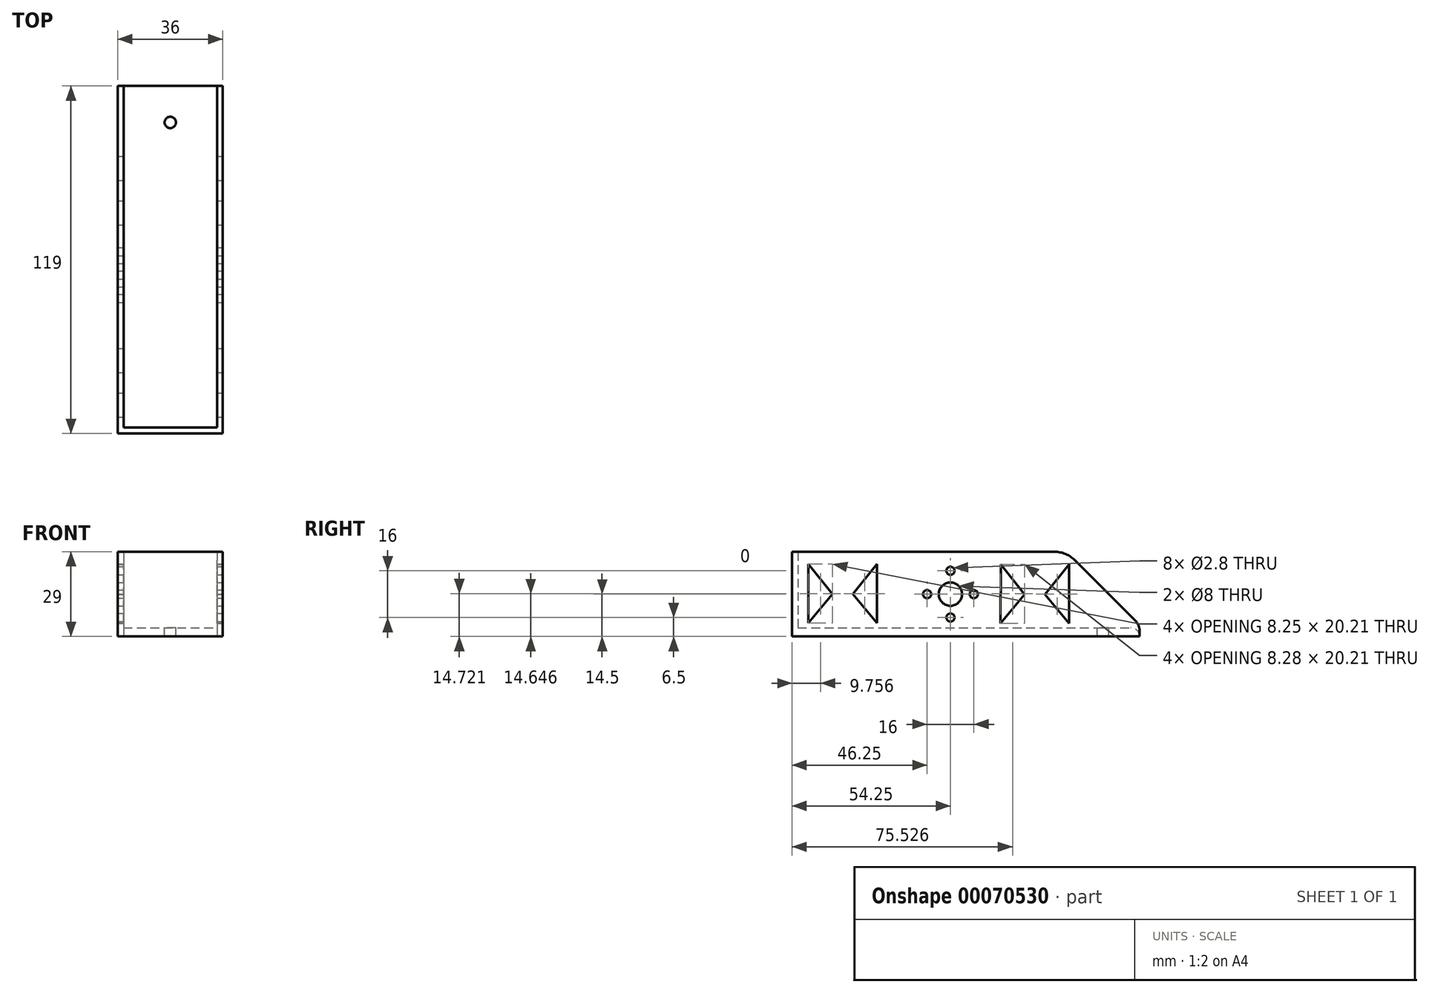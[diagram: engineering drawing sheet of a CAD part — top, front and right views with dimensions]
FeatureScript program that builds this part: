
annotation { "Feature Type Name" : "Feature", "Feature Type Description" : "" }
export const myFeature = defineFeature(function(context is Context, id is Id, definition is map)
    precondition{}
    {
        {
            var Q0;
            Q0=qCreatedBy(makeId("Top.planeOp"),FACE);
            var sketch = newSketch(context, id + "F0", { "sketchPlane" : qUnion([Q0])});
            skLineSegment(sketch, "E0.rect.bottom", {"start": v(-18, -59.5) * mm, "end": v(18, -59.5) * mm});
            skLineSegment(sketch, "E0.rect.top", {"start": v(-18, 59.5) * mm, "end": v(18, 59.5) * mm});
            skLineSegment(sketch, "E0.rect.left", {"start": v(-18, -59.5) * mm, "end": v(-18, 59.5) * mm});
            skLineSegment(sketch, "E0.rect.right", {"start": v(18, -59.5) * mm, "end": v(18, 59.5) * mm});
            skPoint(sketch, "E0.rect.middle", {"position": v(0, 0) * mm});
            skSolve(sketch);
        }
        {
            var Q0;
            Q0=makeQuery(id+"F0.imprint","IMPRINT",FACE,{"disambiguationData":[TD([[makeQuery(id+"F0.imprint","IMPRINT",EDGE,{"derivedFrom":sQuery(id+"F0.wireOp",EDGE,"E0.rect.bottom")}),1.0]])]});
            extrude(context, id + "F1", {"entities" : qUnion([Q0]), "depth" : 3 * mm});
        }
        {
            var Q0;
            Q0=makeQuery(id+"F1.opExtrude","CAP_FACE",FACE,{"disambiguationData":[OSD([sQuery(id+"F0.wireOp",EDGE,"E0.rect.bottom"),sQuery(id+"F0.wireOp",EDGE,"E0.rect.top"),sQuery(id+"F0.wireOp",EDGE,"E0.rect.left"),sQuery(id+"F0.wireOp",EDGE,"E0.rect.right")])],"isStart":false});
            var sketch = newSketch(context, id + "F2", { "sketchPlane" : qUnion([Q0])});
            skLineSegment(sketch, "E1.rect.bottom", {"start": v(-16, -57.5) * mm, "end": v(16, -57.5) * mm});
            skLineSegment(sketch, "E1.rect.left", {"start": v(-16, -57.5) * mm, "end": v(-16, 57.5) * mm});
            skLineSegment(sketch, "E1.rect.right", {"start": v(16, -57.5) * mm, "end": v(16, 57.5) * mm});
            skPoint(sketch, "E1.rect.middle", {"position": v(0, 0) * mm});
            skPoint(sketch, "E2.endSnap0", {"position": v(0, -57.5) * mm});
            skLineSegment(sketch, "E3", {"start": v(16, 57.5) * mm, "end": v(16, 59.5) * mm});
            skLineSegment(sketch, "E4", {"start": v(-16, 57.5) * mm, "end": v(-16, 59.5) * mm});
            skSolve(sketch);
        }
        {
            var Q0;
            Q0=makeQuery(id+"F2.imprint","IMPRINT",FACE,{"disambiguationData":[TD([[makeQuery(id+"F2.imprint","IMPRINT",EDGE,{"derivedFrom":sQuery(id+"F2.wireOp",EDGE,"E1.rect.bottom")}),-1.0]])]});
            extrude(context, id + "F3", {"entities" : qUnion([Q0]), "operationType" : NewBodyOperationType.ADD, "depth" : 26 * mm});
        }
        {
            var Q0;
            Q0=makeQuery(id+"F1.opExtrude","CAP_FACE",FACE,{"disambiguationData":[OSD([sQuery(id+"F0.wireOp",EDGE,"E0.rect.bottom"),sQuery(id+"F0.wireOp",EDGE,"E0.rect.top"),sQuery(id+"F0.wireOp",EDGE,"E0.rect.left"),sQuery(id+"F0.wireOp",EDGE,"E0.rect.right")])],"isStart":false});
            var sketch = newSketch(context, id + "F4", { "sketchPlane" : qUnion([Q0])});
            skLineSegment(sketch, "E5", {"start": v(0, -57.5) * mm, "end": v(0, 47) * mm, "construction": true});
            skPoint(sketch, "E5.endSnap0", {"position": v(0, -57.5) * mm});
            skArc(sketch, "E6", {"start": v(-3.7, 45.5) * mm, "mid": v(0, 43) * mm, "end": v(3.7, 45.5) * mm});
            skCircle(sketch, "E7", {"center": v(0, 47) * mm, "radius": 1.95 * mm});
            skLineSegment(sketch, "E8.rect.bottom", {"start": v(-4, 45.5) * mm, "end": v(-1.25, 45.5) * mm});
            skLineSegment(sketch, "E8.rect.top", {"start": v(-4, 48.5) * mm, "end": v(-1.25, 48.5) * mm});
            skLineSegment(sketch, "E8.rect.left", {"start": v(-4, 45.5) * mm, "end": v(-4, 48.5) * mm});
            skLineSegment(sketch, "E8.rect.right", {"start": v(4, 45.5) * mm, "end": v(4, 48.5) * mm});
            skArc(sketch, "E9.trimOffspring", {"start": v(3.7, 48.5) * mm, "mid": v(0, 51) * mm, "end": v(-3.7, 48.5) * mm});
            skLineSegment(sketch, "E10.trimOffspring", {"start": v(1.25, 45.5) * mm, "end": v(4, 45.5) * mm});
            skLineSegment(sketch, "E11.trimOffspring", {"start": v(1.25, 48.5) * mm, "end": v(4, 48.5) * mm});
            skSolve(sketch);
        }
        {
            var Q0;
            {var subQ0=sQuery(id+"F0.wireOp",EDGE,"E0.rect.top");var subQ1=makeQuery(id+"F1.opExtrude","CAP_EDGE",EDGE,{"disambiguationData":[OSD([subQ0])],"isStart":false});Q0=makeQuery(id+"F3.opExtrude","CAP_EDGE",EDGE,{"disambiguationData":[OSD([subQ0]),TDD([makeQuery(id+"F2.imprint","IMPRINT",EDGE,{"disambiguationData":[TD([[makeQuery(id+"F2.imprint","INTERSECT",VERTEX,{"derivedFrom":[subQ1,makeQuery(id+"F1.opExtrude","CAP_EDGE",EDGE,{"disambiguationData":[OSD([sQuery(id+"F0.wireOp",EDGE,"E0.rect.left")])],"isStart":false})]}),-1.0]])],"derivedFrom":subQ1})])],"isStart":false});}
            var Q1;
            {var subQ0=sQuery(id+"F0.wireOp",EDGE,"E0.rect.top");var subQ1=makeQuery(id+"F1.opExtrude","CAP_EDGE",EDGE,{"disambiguationData":[OSD([subQ0])],"isStart":false});Q1=makeQuery(id+"F3.opExtrude","CAP_EDGE",EDGE,{"disambiguationData":[OSD([subQ0]),TDD([makeQuery(id+"F2.imprint","IMPRINT",EDGE,{"disambiguationData":[TD([[makeQuery(id+"F2.imprint","INTERSECT",VERTEX,{"derivedFrom":[subQ1,makeQuery(id+"F1.opExtrude","CAP_EDGE",EDGE,{"disambiguationData":[OSD([sQuery(id+"F0.wireOp",EDGE,"E0.rect.right")])],"isStart":false})]}),1.0]])],"derivedFrom":subQ1})])],"isStart":false});}
            chamfer(context, id + "F5", {"entities" : qUnion([Q0, Q1]), "width" : 25 * mm, "tangentPropagation" : true});
        }
        {
            var Q0;
            {var subQ0=sQuery(id+"F2.wireOp",EDGE,"E3");var subQ1=sQuery(id+"F0.wireOp",EDGE,"E0.rect.right");var subQ2=sQuery(id+"F0.wireOp",EDGE,"E0.rect.top");var subQ3=makeQuery(id+"F1.opExtrude","CAP_EDGE",EDGE,{"disambiguationData":[OSD([subQ2])],"isStart":false});Q0=makeQuery(id+"F5.opChamfer","BLEND_EDGE",EDGE,{"blendedFrom":[makeQuery(id+"F3.opExtrude","CAP_EDGE",EDGE,{"disambiguationData":[OSD([subQ2]),TDD([makeQuery(id+"F2.imprint","IMPRINT",EDGE,{"disambiguationData":[TD([[makeQuery(id+"F2.imprint","INTERSECT",VERTEX,{"derivedFrom":[subQ3,makeQuery(id+"F1.opExtrude","CAP_EDGE",EDGE,{"disambiguationData":[OSD([subQ1])],"isStart":false})]}),1.0]])],"derivedFrom":subQ3})])],"isStart":false}),makeQuery(id+"F3.opExtrude","CAP_FACE",FACE,{"disambiguationData":[OSD([sQuery(id+"F0.wireOp",EDGE,"E0.rect.bottom"),subQ2,sQuery(id+"F0.wireOp",EDGE,"E0.rect.left"),subQ1,sQuery(id+"F2.wireOp",EDGE,"E1.rect.bottom"),sQuery(id+"F2.wireOp",EDGE,"E1.rect.left"),sQuery(id+"F2.wireOp",EDGE,"E1.rect.right"),subQ0,sQuery(id+"F2.wireOp",EDGE,"E4")])],"isStart":false})],"blendedInto":[makeQuery(id+"F3.opExtrude","CAP_FACE",FACE,{"disambiguationData":[OSD([sQuery(id+"F0.wireOp",EDGE,"E0.rect.bottom"),subQ2,sQuery(id+"F0.wireOp",EDGE,"E0.rect.left"),subQ1,sQuery(id+"F2.wireOp",EDGE,"E1.rect.bottom"),sQuery(id+"F2.wireOp",EDGE,"E1.rect.left"),sQuery(id+"F2.wireOp",EDGE,"E1.rect.right"),subQ0,sQuery(id+"F2.wireOp",EDGE,"E4")])],"isStart":false})]});}
            var Q1;
            {var subQ0=sQuery(id+"F2.wireOp",EDGE,"E4");var subQ1=sQuery(id+"F0.wireOp",EDGE,"E0.rect.left");var subQ2=sQuery(id+"F0.wireOp",EDGE,"E0.rect.top");var subQ3=makeQuery(id+"F1.opExtrude","CAP_EDGE",EDGE,{"disambiguationData":[OSD([subQ2])],"isStart":false});Q1=makeQuery(id+"F5.opChamfer","BLEND_EDGE",EDGE,{"blendedFrom":[makeQuery(id+"F3.opExtrude","CAP_EDGE",EDGE,{"disambiguationData":[OSD([subQ2]),TDD([makeQuery(id+"F2.imprint","IMPRINT",EDGE,{"disambiguationData":[TD([[makeQuery(id+"F2.imprint","INTERSECT",VERTEX,{"derivedFrom":[subQ3,makeQuery(id+"F1.opExtrude","CAP_EDGE",EDGE,{"disambiguationData":[OSD([subQ1])],"isStart":false})]}),-1.0]])],"derivedFrom":subQ3})])],"isStart":false}),makeQuery(id+"F3.opExtrude","CAP_FACE",FACE,{"disambiguationData":[OSD([sQuery(id+"F0.wireOp",EDGE,"E0.rect.bottom"),subQ2,subQ1,sQuery(id+"F0.wireOp",EDGE,"E0.rect.right"),sQuery(id+"F2.wireOp",EDGE,"E1.rect.bottom"),sQuery(id+"F2.wireOp",EDGE,"E1.rect.left"),sQuery(id+"F2.wireOp",EDGE,"E1.rect.right"),sQuery(id+"F2.wireOp",EDGE,"E3"),subQ0])],"isStart":false})],"blendedInto":[makeQuery(id+"F3.opExtrude","CAP_FACE",FACE,{"disambiguationData":[OSD([sQuery(id+"F0.wireOp",EDGE,"E0.rect.bottom"),subQ2,subQ1,sQuery(id+"F0.wireOp",EDGE,"E0.rect.right"),sQuery(id+"F2.wireOp",EDGE,"E1.rect.bottom"),sQuery(id+"F2.wireOp",EDGE,"E1.rect.left"),sQuery(id+"F2.wireOp",EDGE,"E1.rect.right"),sQuery(id+"F2.wireOp",EDGE,"E3"),subQ0])],"isStart":false})]});}
            fillet(context, id + "F6", {"entities" : qUnion([Q0, Q1]), "radius" : 10 * mm, "tangentPropagation" : true, "allowEdgeOverflow" : false});
        }
        {
            var Q0;
            Q0=makeQuery(id+"F1.opExtrude","CAP_EDGE",EDGE,{"disambiguationData":[OSD([sQuery(id+"F0.wireOp",EDGE,"E0.rect.top")])],"isStart":false});
            fillet(context, id + "F7", {"entities" : qUnion([Q0]), "radius" : 3 * mm, "tangentPropagation" : true, "allowEdgeOverflow" : false});
        }
        {
            var Q0;
            {var subQ0=sQuery(id+"F0.wireOp",EDGE,"E0.rect.top");var subQ1=makeQuery(id+"F1.opExtrude","CAP_EDGE",EDGE,{"disambiguationData":[OSD([subQ0])],"isStart":false});var subQ2=makeQuery(id+"F2.imprint","IMPRINT",EDGE,{"disambiguationData":[TD([[makeQuery(id+"F2.imprint","INTERSECT",VERTEX,{"derivedFrom":[subQ1,makeQuery(id+"F1.opExtrude","CAP_EDGE",EDGE,{"disambiguationData":[OSD([sQuery(id+"F0.wireOp",EDGE,"E0.rect.right")])],"isStart":false})]}),1.0]])],"derivedFrom":subQ1});Q0=makeQuery(id+"F5.opChamfer","BLEND_EDGE",EDGE,{"blendedFrom":[makeQuery(id+"F3.opExtrude","CAP_EDGE",EDGE,{"disambiguationData":[OSD([subQ0]),TDD([subQ2])],"isStart":false}),makeQuery(id+"F3.boolean.opBoolean","MERGE",FACE,{"derivedFrom":[makeQuery(id+"F1.opExtrude","SWEPT_FACE",FACE,{"disambiguationData":[OSD([subQ0])]}),makeQuery(id+"F3.opExtrude","SWEPT_FACE",FACE,{"disambiguationData":[OSD([subQ0]),TDD([makeQuery(id+"F2.imprint","IMPRINT",EDGE,{"disambiguationData":[TD([[makeQuery(id+"F2.imprint","INTERSECT",VERTEX,{"derivedFrom":[subQ1,makeQuery(id+"F1.opExtrude","CAP_EDGE",EDGE,{"disambiguationData":[OSD([sQuery(id+"F0.wireOp",EDGE,"E0.rect.left")])],"isStart":false})]}),-1.0]])],"derivedFrom":subQ1})])]}),makeQuery(id+"F3.opExtrude","SWEPT_FACE",FACE,{"disambiguationData":[OSD([subQ0]),TDD([subQ2])]})]})],"blendedInto":[makeQuery(id+"F3.boolean.opBoolean","MERGE",FACE,{"derivedFrom":[makeQuery(id+"F1.opExtrude","SWEPT_FACE",FACE,{"disambiguationData":[OSD([subQ0])]}),makeQuery(id+"F3.opExtrude","SWEPT_FACE",FACE,{"disambiguationData":[OSD([subQ0]),TDD([makeQuery(id+"F2.imprint","IMPRINT",EDGE,{"disambiguationData":[TD([[makeQuery(id+"F2.imprint","INTERSECT",VERTEX,{"derivedFrom":[subQ1,makeQuery(id+"F1.opExtrude","CAP_EDGE",EDGE,{"disambiguationData":[OSD([sQuery(id+"F0.wireOp",EDGE,"E0.rect.left")])],"isStart":false})]}),-1.0]])],"derivedFrom":subQ1})])]}),makeQuery(id+"F3.opExtrude","SWEPT_FACE",FACE,{"disambiguationData":[OSD([subQ0]),TDD([subQ2])]})]})]});}
            var Q1;
            {var subQ0=sQuery(id+"F0.wireOp",EDGE,"E0.rect.top");var subQ1=makeQuery(id+"F1.opExtrude","CAP_EDGE",EDGE,{"disambiguationData":[OSD([subQ0])],"isStart":false});var subQ2=makeQuery(id+"F2.imprint","IMPRINT",EDGE,{"disambiguationData":[TD([[makeQuery(id+"F2.imprint","INTERSECT",VERTEX,{"derivedFrom":[subQ1,makeQuery(id+"F1.opExtrude","CAP_EDGE",EDGE,{"disambiguationData":[OSD([sQuery(id+"F0.wireOp",EDGE,"E0.rect.left")])],"isStart":false})]}),-1.0]])],"derivedFrom":subQ1});Q1=makeQuery(id+"F5.opChamfer","BLEND_EDGE",EDGE,{"blendedFrom":[makeQuery(id+"F3.opExtrude","CAP_EDGE",EDGE,{"disambiguationData":[OSD([subQ0]),TDD([subQ2])],"isStart":false}),makeQuery(id+"F3.boolean.opBoolean","MERGE",FACE,{"derivedFrom":[makeQuery(id+"F1.opExtrude","SWEPT_FACE",FACE,{"disambiguationData":[OSD([subQ0])]}),makeQuery(id+"F3.opExtrude","SWEPT_FACE",FACE,{"disambiguationData":[OSD([subQ0]),TDD([subQ2])]}),makeQuery(id+"F3.opExtrude","SWEPT_FACE",FACE,{"disambiguationData":[OSD([subQ0]),TDD([makeQuery(id+"F2.imprint","IMPRINT",EDGE,{"disambiguationData":[TD([[makeQuery(id+"F2.imprint","INTERSECT",VERTEX,{"derivedFrom":[subQ1,makeQuery(id+"F1.opExtrude","CAP_EDGE",EDGE,{"disambiguationData":[OSD([sQuery(id+"F0.wireOp",EDGE,"E0.rect.right")])],"isStart":false})]}),1.0]])],"derivedFrom":subQ1})])]})]})],"blendedInto":[makeQuery(id+"F3.boolean.opBoolean","MERGE",FACE,{"derivedFrom":[makeQuery(id+"F1.opExtrude","SWEPT_FACE",FACE,{"disambiguationData":[OSD([subQ0])]}),makeQuery(id+"F3.opExtrude","SWEPT_FACE",FACE,{"disambiguationData":[OSD([subQ0]),TDD([subQ2])]}),makeQuery(id+"F3.opExtrude","SWEPT_FACE",FACE,{"disambiguationData":[OSD([subQ0]),TDD([makeQuery(id+"F2.imprint","IMPRINT",EDGE,{"disambiguationData":[TD([[makeQuery(id+"F2.imprint","INTERSECT",VERTEX,{"derivedFrom":[subQ1,makeQuery(id+"F1.opExtrude","CAP_EDGE",EDGE,{"disambiguationData":[OSD([sQuery(id+"F0.wireOp",EDGE,"E0.rect.right")])],"isStart":false})]}),1.0]])],"derivedFrom":subQ1})])]})]})]});}
            fillet(context, id + "F8", {"entities" : qUnion([Q0, Q1]), "radius" : 5 * mm, "tangentPropagation" : true, "allowEdgeOverflow" : false});
        }
        {
            var Q0;
            {var subQ0=sQuery(id+"F0.wireOp",EDGE,"E0.rect.right");Q0=makeQuery(id+"F3.boolean.opBoolean","MERGE",FACE,{"derivedFrom":[makeQuery(id+"F1.opExtrude","SWEPT_FACE",FACE,{"disambiguationData":[OSD([subQ0])]}),makeQuery(id+"F3.opExtrude","SWEPT_FACE",FACE,{"disambiguationData":[OSD([subQ0])]})]});}
            var sketch = newSketch(context, id + "F9", { "sketchPlane" : qUnion([Q0])});
            skLineSegment(sketch, "E12", {"start": v(-59.5, 14.5) * mm, "end": v(49, 14.5) * mm, "construction": true});
            skCircle(sketch, "E13", {"center": v(-5.25, 14.5) * mm, "radius": 4 * mm});
            skLineSegment(sketch, "E14", {"start": v(-5.25, 14.5) * mm, "end": v(-5.25, 22.5) * mm, "construction": true});
            skCircle(sketch, "E15", {"center": v(-5.25, 22.5) * mm, "radius": 1.4 * mm});
            skCircle(sketch, "E16.1.0", {"center": v(-13.25, 14.5) * mm, "radius": 1.4 * mm});
            skCircle(sketch, "E16.2.0", {"center": v(-5.25, 6.5) * mm, "radius": 1.4 * mm});
            skCircle(sketch, "E16.3.0", {"center": v(2.75, 14.5) * mm, "radius": 1.4 * mm});
            skLineSegment(sketch, "E17", {"start": v(-53.87, 24.83) * mm, "end": v(-53.87, 4.61) * mm});
            skLineSegment(sketch, "E18", {"start": v(-53.87, 4.61) * mm, "end": v(-45.62, 14.5) * mm});
            skLineSegment(sketch, "E19", {"start": v(-45.62, 14.5) * mm, "end": v(-53.87, 24.83) * mm});
            skLineSegment(sketch, "E20", {"start": v(-42.14, 26.12) * mm, "end": v(-42.14, 3.8) * mm, "construction": true});
            skLineSegment(sketch, "E21.MirrorCS", {"start": v(-38.67, 14.5) * mm, "end": v(-30.42, 24.83) * mm});
            skLineSegment(sketch, "E22.MirrorCS", {"start": v(-30.42, 24.83) * mm, "end": v(-30.42, 4.61) * mm});
            skLineSegment(sketch, "E23.MirrorCS", {"start": v(-30.42, 4.61) * mm, "end": v(-38.67, 14.5) * mm});
            skLineSegment(sketch, "E24", {"start": v(-9.23, 23.24) * mm, "end": v(-9.27, 3.92) * mm, "construction": true});
            skLineSegment(sketch, "E25.MirrorCS", {"start": v(23.68, 26) * mm, "end": v(23.6, 3.69) * mm, "construction": true});
            skLineSegment(sketch, "E26.MirrorCS", {"start": v(20.17, 14.4) * mm, "end": v(11.96, 24.75) * mm});
            skLineSegment(sketch, "E27.MirrorCS", {"start": v(27.12, 14.37) * mm, "end": v(35.4, 24.67) * mm});
            skLineSegment(sketch, "E28.MirrorCS", {"start": v(35.33, 4.46) * mm, "end": v(27.12, 14.37) * mm});
            skLineSegment(sketch, "E29.MirrorCS", {"start": v(41, 14.32) * mm, "end": v(-67.5, 14.7) * mm, "construction": true});
            skLineSegment(sketch, "E30.MirrorCS", {"start": v(11.88, 4.54) * mm, "end": v(20.17, 14.4) * mm});
            skLineSegment(sketch, "E31.MirrorCS", {"start": v(11.96, 24.75) * mm, "end": v(11.88, 4.54) * mm});
            skLineSegment(sketch, "E32.MirrorCS", {"start": v(35.4, 24.67) * mm, "end": v(35.33, 4.46) * mm});
            skSolve(sketch);
        }
        {
            var Q0;
            Q0=makeQuery(id+"F4.imprint","IMPRINT",FACE,{"disambiguationData":[TD([[makeQuery(id+"F4.imprint","IMPRINT",EDGE,{"derivedFrom":sQuery(id+"F4.wireOp",EDGE,"E7")}),1.0]])]});
            extrude(context, id + "F10", {"entities" : qUnion([Q0]), "operationType" : NewBodyOperationType.REMOVE, "oppositeDirection" : true, "depth" : 25 * mm});
        }
        {
            var Q0;
            Q0=makeQuery(id+"F9.imprint","IMPRINT",FACE,{"disambiguationData":[TD([[makeQuery(id+"F9.imprint","IMPRINT",EDGE,{"derivedFrom":sQuery(id+"F9.wireOp",EDGE,"E15")}),1.0]])]});
            var Q1;
            Q1=makeQuery(id+"F9.imprint","IMPRINT",FACE,{"disambiguationData":[TD([[makeQuery(id+"F9.imprint","IMPRINT",EDGE,{"derivedFrom":sQuery(id+"F9.wireOp",EDGE,"E16.3.0")}),1.0]])]});
            var Q2;
            Q2=makeQuery(id+"F9.imprint","IMPRINT",FACE,{"disambiguationData":[TD([[makeQuery(id+"F9.imprint","IMPRINT",EDGE,{"derivedFrom":sQuery(id+"F9.wireOp",EDGE,"E13")}),1.0]])]});
            var Q3;
            Q3=makeQuery(id+"F9.imprint","IMPRINT",FACE,{"disambiguationData":[TD([[makeQuery(id+"F9.imprint","IMPRINT",EDGE,{"derivedFrom":sQuery(id+"F9.wireOp",EDGE,"E16.2.0")}),1.0]])]});
            var Q4;
            Q4=makeQuery(id+"F9.imprint","IMPRINT",FACE,{"disambiguationData":[TD([[makeQuery(id+"F9.imprint","IMPRINT",EDGE,{"derivedFrom":sQuery(id+"F9.wireOp",EDGE,"E16.1.0")}),1.0]])]});
            var Q5;
            Q5=makeQuery(id+"F9.imprint","IMPRINT",FACE,{"disambiguationData":[TD([[makeQuery(id+"F9.imprint","IMPRINT",EDGE,{"derivedFrom":sQuery(id+"F9.wireOp",EDGE,"E17")}),1.0]])]});
            var Q6;
            Q6=makeQuery(id+"F9.imprint","IMPRINT",FACE,{"disambiguationData":[TD([[makeQuery(id+"F9.imprint","IMPRINT",EDGE,{"derivedFrom":sQuery(id+"F9.wireOp",EDGE,"E21.MirrorCS")}),-1.0]])]});
            var Q7;
            Q7=makeQuery(id+"F9.imprint","IMPRINT",FACE,{"disambiguationData":[TD([[makeQuery(id+"F9.imprint","IMPRINT",EDGE,{"derivedFrom":sQuery(id+"F9.wireOp",EDGE,"E26.MirrorCS")}),1.0]])]});
            var Q8;
            Q8=makeQuery(id+"F9.imprint","IMPRINT",FACE,{"disambiguationData":[TD([[makeQuery(id+"F9.imprint","IMPRINT",EDGE,{"derivedFrom":sQuery(id+"F9.wireOp",EDGE,"E27.MirrorCS")}),-1.0]])]});
            extrude(context, id + "F11", {"entities" : qUnion([Q0, Q1, Q2, Q3, Q4, Q5, Q6, Q7, Q8]), "operationType" : NewBodyOperationType.REMOVE, "endBound" : BoundingType.THROUGH_ALL, "oppositeDirection" : true, "depth" : 25 * mm});
        }
    });
